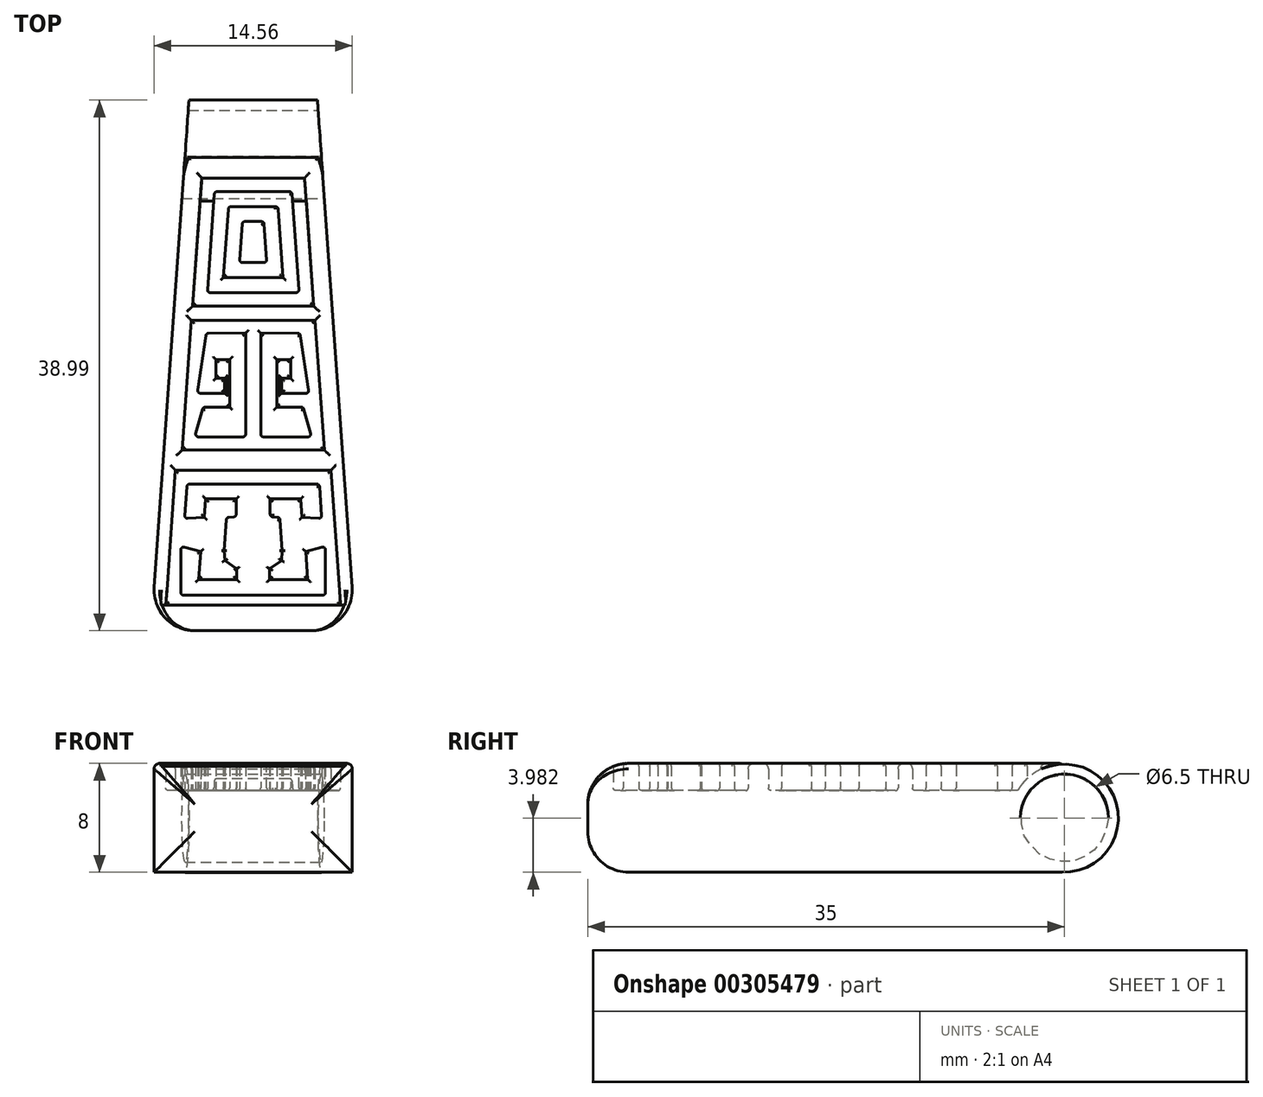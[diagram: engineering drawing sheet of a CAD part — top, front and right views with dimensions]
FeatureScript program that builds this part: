
annotation { "Feature Type Name" : "Feature", "Feature Type Description" : "" }
export const myFeature = defineFeature(function(context is Context, id is Id, definition is map)
    precondition{}
    {
        {
            var Q0;
            Q0=qCreatedBy(makeId("Top.planeOp"),FACE);
            var sketch = newSketch(context, id + "F0", { "sketchPlane" : qUnion([Q0])});
            skLineSegment(sketch, "E0", {"start": v(0, 0) * mm, "end": v(5, 0) * mm});
            skLineSegment(sketch, "E1", {"start": v(5, 0) * mm, "end": v(7.5, -35) * mm});
            skLineSegment(sketch, "E2", {"start": v(7.5, -35) * mm, "end": v(0, -35) * mm});
            skLineSegment(sketch, "E3", {"start": v(0, 0) * mm, "end": v(0, -35) * mm, "construction": true});
            skLineSegment(sketch, "E4", {"start": v(0, -1.73) * mm, "end": v(3.77, -1.73) * mm});
            skLineSegment(sketch, "E5", {"start": v(3.77, -1.73) * mm, "end": v(4.44, -11.15) * mm});
            skLineSegment(sketch, "E6", {"start": v(4.44, -11.15) * mm, "end": v(0, -11.15) * mm});
            skLineSegment(sketch, "E7", {"start": v(0, -12.2) * mm, "end": v(4.54, -12.2) * mm});
            skLineSegment(sketch, "E8", {"start": v(4.54, -12.2) * mm, "end": v(5.22, -21.73) * mm});
            skLineSegment(sketch, "E9", {"start": v(5.22, -21.73) * mm, "end": v(0, -21.73) * mm});
            skLineSegment(sketch, "E10", {"start": v(0, -23.21) * mm, "end": v(5.7, -23.21) * mm});
            skLineSegment(sketch, "E11", {"start": v(5.7, -23.21) * mm, "end": v(6.42, -33.12) * mm});
            skLineSegment(sketch, "E12", {"start": v(6.42, -33.12) * mm, "end": v(0, -33.12) * mm});
            skLineSegment(sketch, "E13.MirrorCS", {"start": v(0, 0) * mm, "end": v(-5, 0) * mm});
            skLineSegment(sketch, "E14.MirrorCS", {"start": v(-4.44, -11.15) * mm, "end": v(0, -11.15) * mm});
            skLineSegment(sketch, "E15.MirrorCS", {"start": v(-7.5, -35) * mm, "end": v(0, -35) * mm});
            skLineSegment(sketch, "E16.MirrorCS", {"start": v(-6.42, -33.12) * mm, "end": v(0, -33.12) * mm});
            skLineSegment(sketch, "E17.MirrorCS", {"start": v(-5.7, -23.21) * mm, "end": v(-6.42, -33.12) * mm});
            skLineSegment(sketch, "E18.MirrorCS", {"start": v(-5, 0) * mm, "end": v(-7.5, -35) * mm});
            skLineSegment(sketch, "E19.MirrorCS", {"start": v(0, -23.21) * mm, "end": v(-5.7, -23.21) * mm});
            skLineSegment(sketch, "E20.MirrorCS", {"start": v(-3.77, -1.73) * mm, "end": v(-4.44, -11.15) * mm});
            skLineSegment(sketch, "E21.MirrorCS", {"start": v(-5.22, -21.73) * mm, "end": v(0, -21.73) * mm});
            skLineSegment(sketch, "E22.MirrorCS", {"start": v(0, -12.2) * mm, "end": v(-4.54, -12.2) * mm});
            skLineSegment(sketch, "E23.MirrorCS", {"start": v(-4.54, -12.2) * mm, "end": v(-5.22, -21.73) * mm});
            skLineSegment(sketch, "E24.MirrorCS", {"start": v(0, -1.73) * mm, "end": v(-3.77, -1.73) * mm});
            skLineSegment(sketch, "E25.0", {"start": v(0, -2.73) * mm, "end": v(2.84, -2.73) * mm});
            skLineSegment(sketch, "E25.1", {"start": v(-2.84, -2.73) * mm, "end": v(-3.37, -10.15) * mm});
            skLineSegment(sketch, "E25.2", {"start": v(-3.37, -10.15) * mm, "end": v(0, -10.15) * mm});
            skLineSegment(sketch, "E25.3", {"start": v(0, -2.73) * mm, "end": v(-2.84, -2.73) * mm});
            skLineSegment(sketch, "E25.4", {"start": v(3.37, -10.15) * mm, "end": v(0, -10.15) * mm});
            skLineSegment(sketch, "E25.5", {"start": v(2.84, -2.73) * mm, "end": v(3.37, -10.15) * mm});
            skLineSegment(sketch, "E26.0", {"start": v(0, -3.83) * mm, "end": v(-1.82, -3.83) * mm});
            skLineSegment(sketch, "E26.1", {"start": v(1.82, -3.83) * mm, "end": v(2.19, -9.05) * mm});
            skLineSegment(sketch, "E26.2", {"start": v(2.19, -9.05) * mm, "end": v(0.29, -9.05) * mm});
            skLineSegment(sketch, "E26.3", {"start": v(0, -3.83) * mm, "end": v(1.82, -3.83) * mm});
            skLineSegment(sketch, "E26.4", {"start": v(-2.19, -9.05) * mm, "end": v(0.29, -9.05) * mm});
            skLineSegment(sketch, "E26.5", {"start": v(-1.82, -3.83) * mm, "end": v(-2.19, -9.05) * mm});
            skLineSegment(sketch, "E27", {"start": v(0.55, -13.13) * mm, "end": v(0.55, -20.76) * mm});
            skLineSegment(sketch, "E28", {"start": v(0.55, -20.76) * mm, "end": v(4.28, -20.76) * mm});
            skLineSegment(sketch, "E29", {"start": v(4.28, -20.76) * mm, "end": v(3.68, -18.57) * mm});
            skLineSegment(sketch, "E30", {"start": v(3.68, -18.57) * mm, "end": v(1.73, -18.57) * mm});
            skLineSegment(sketch, "E31", {"start": v(1.73, -18.57) * mm, "end": v(1.73, -15.07) * mm});
            skLineSegment(sketch, "E32", {"start": v(1.73, -15.07) * mm, "end": v(2.74, -15.07) * mm});
            skLineSegment(sketch, "E33", {"start": v(2.74, -15.07) * mm, "end": v(2.74, -16.45) * mm});
            skLineSegment(sketch, "E34", {"start": v(2.74, -16.45) * mm, "end": v(2.09, -16.45) * mm});
            skLineSegment(sketch, "E35", {"start": v(2.09, -16.45) * mm, "end": v(2.09, -17.55) * mm});
            skLineSegment(sketch, "E36", {"start": v(2.09, -17.55) * mm, "end": v(4.1, -17.55) * mm});
            skLineSegment(sketch, "E37", {"start": v(4.1, -17.55) * mm, "end": v(3.44, -13.14) * mm});
            skLineSegment(sketch, "E38", {"start": v(3.44, -13.14) * mm, "end": v(0.55, -13.13) * mm});
            skLineSegment(sketch, "E39.MirrorCS", {"start": v(-1.73, -15.07) * mm, "end": v(-2.74, -15.07) * mm});
            skLineSegment(sketch, "E40.MirrorCS", {"start": v(-0.55, -20.76) * mm, "end": v(-4.28, -20.76) * mm});
            skLineSegment(sketch, "E41.MirrorCS", {"start": v(-4.1, -17.55) * mm, "end": v(-3.44, -13.14) * mm});
            skLineSegment(sketch, "E42.MirrorCS", {"start": v(-1.73, -18.57) * mm, "end": v(-1.73, -15.07) * mm});
            skLineSegment(sketch, "E43.MirrorCS", {"start": v(-2.09, -17.55) * mm, "end": v(-4.1, -17.55) * mm});
            skLineSegment(sketch, "E44.MirrorCS", {"start": v(-3.44, -13.14) * mm, "end": v(-0.55, -13.13) * mm});
            skLineSegment(sketch, "E45.MirrorCS", {"start": v(-2.09, -16.45) * mm, "end": v(-2.09, -17.55) * mm});
            skLineSegment(sketch, "E46.MirrorCS", {"start": v(-2.74, -15.07) * mm, "end": v(-2.74, -16.45) * mm});
            skLineSegment(sketch, "E47.MirrorCS", {"start": v(-0.55, -13.13) * mm, "end": v(-0.55, -20.76) * mm});
            skLineSegment(sketch, "E48.MirrorCS", {"start": v(-3.68, -18.57) * mm, "end": v(-1.73, -18.57) * mm});
            skLineSegment(sketch, "E49.MirrorCS", {"start": v(-2.74, -16.45) * mm, "end": v(-2.09, -16.45) * mm});
            skLineSegment(sketch, "E50.MirrorCS", {"start": v(-4.28, -20.76) * mm, "end": v(-3.68, -18.57) * mm});
            skLineSegment(sketch, "E51", {"start": v(0, -24.23) * mm, "end": v(4.86, -24.23) * mm});
            skLineSegment(sketch, "E52", {"start": v(4.86, -24.23) * mm, "end": v(5.04, -26.76) * mm});
            skLineSegment(sketch, "E53", {"start": v(5.04, -26.76) * mm, "end": v(3.6, -26.66) * mm});
            skLineSegment(sketch, "E54", {"start": v(3.6, -26.66) * mm, "end": v(3.5, -25.32) * mm});
            skLineSegment(sketch, "E55", {"start": v(3.5, -25.32) * mm, "end": v(1.25, -25.32) * mm});
            skLineSegment(sketch, "E56", {"start": v(1.25, -25.32) * mm, "end": v(1.25, -26.62) * mm});
            skLineSegment(sketch, "E57", {"start": v(1.25, -26.62) * mm, "end": v(1.96, -26.67) * mm});
            skLineSegment(sketch, "E58", {"start": v(1.96, -26.67) * mm, "end": v(2.13, -29.11) * mm});
            skLineSegment(sketch, "E59", {"start": v(2.13, -29.11) * mm, "end": v(2.08, -29.84) * mm});
            skLineSegment(sketch, "E60", {"start": v(2.08, -29.84) * mm, "end": v(1.2, -30.44) * mm});
            skLineSegment(sketch, "E61", {"start": v(1.2, -30.44) * mm, "end": v(1.2, -31.23) * mm});
            skLineSegment(sketch, "E62", {"start": v(1.2, -31.23) * mm, "end": v(4, -31.23) * mm});
            skLineSegment(sketch, "E63", {"start": v(4, -31.23) * mm, "end": v(3.86, -29.17) * mm});
            skLineSegment(sketch, "E64", {"start": v(3.86, -29.17) * mm, "end": v(5.3, -28.8) * mm});
            skLineSegment(sketch, "E65", {"start": v(5.3, -28.8) * mm, "end": v(5.3, -32.4) * mm});
            skLineSegment(sketch, "E66", {"start": v(5.3, -32.4) * mm, "end": v(0, -32.4) * mm});
            skLineSegment(sketch, "E67.MirrorCS", {"start": v(-1.25, -26.62) * mm, "end": v(-1.96, -26.67) * mm});
            skLineSegment(sketch, "E68.MirrorCS", {"start": v(-5.3, -28.8) * mm, "end": v(-5.3, -32.4) * mm});
            skLineSegment(sketch, "E69.MirrorCS", {"start": v(-1.96, -26.67) * mm, "end": v(-2.13, -29.11) * mm});
            skLineSegment(sketch, "E70.MirrorCS", {"start": v(-3.86, -29.17) * mm, "end": v(-5.3, -28.8) * mm});
            skLineSegment(sketch, "E71.MirrorCS", {"start": v(-4, -31.23) * mm, "end": v(-3.86, -29.17) * mm});
            skLineSegment(sketch, "E72.MirrorCS", {"start": v(-4.86, -24.23) * mm, "end": v(-5.04, -26.76) * mm});
            skLineSegment(sketch, "E73.MirrorCS", {"start": v(-2.13, -29.11) * mm, "end": v(-2.08, -29.84) * mm});
            skLineSegment(sketch, "E74.MirrorCS", {"start": v(-1.25, -25.32) * mm, "end": v(-1.25, -26.62) * mm});
            skLineSegment(sketch, "E75.MirrorCS", {"start": v(-1.2, -30.44) * mm, "end": v(-1.2, -31.23) * mm});
            skLineSegment(sketch, "E76.MirrorCS", {"start": v(-3.6, -26.66) * mm, "end": v(-3.5, -25.32) * mm});
            skLineSegment(sketch, "E77.MirrorCS", {"start": v(-5.04, -26.76) * mm, "end": v(-3.6, -26.66) * mm});
            skLineSegment(sketch, "E78.MirrorCS", {"start": v(-2.08, -29.84) * mm, "end": v(-1.2, -30.44) * mm});
            skLineSegment(sketch, "E79.MirrorCS", {"start": v(-1.2, -31.23) * mm, "end": v(-4, -31.23) * mm});
            skLineSegment(sketch, "E80.MirrorCS", {"start": v(-3.5, -25.32) * mm, "end": v(-1.25, -25.32) * mm});
            skLineSegment(sketch, "E81.MirrorCS", {"start": v(0, -24.23) * mm, "end": v(-4.86, -24.23) * mm});
            skLineSegment(sketch, "E82.MirrorCS", {"start": v(-5.3, -32.4) * mm, "end": v(0, -32.4) * mm});
            skLineSegment(sketch, "E83.0", {"start": v(0, -4.93) * mm, "end": v(0.8, -4.93) * mm});
            skLineSegment(sketch, "E83.1", {"start": v(-0.8, -4.93) * mm, "end": v(-1, -7.95) * mm});
            skLineSegment(sketch, "E83.2", {"start": v(-1, -7.95) * mm, "end": v(0, -7.95) * mm});
            skLineSegment(sketch, "E83.3", {"start": v(0, -4.93) * mm, "end": v(-0.8, -4.93) * mm});
            skLineSegment(sketch, "E83.4", {"start": v(1, -7.95) * mm, "end": v(0, -7.95) * mm});
            skLineSegment(sketch, "E83.5", {"start": v(0.8, -4.93) * mm, "end": v(1, -7.95) * mm});
            skSolve(sketch);
        }
        {
            var Q0;
            Q0=makeQuery(id+"F0.imprint","IMPRINT",FACE,{"disambiguationData":[TD([[makeQuery(id+"F0.imprint","IMPRINT",EDGE,{"derivedFrom":sQuery(id+"F0.wireOp",EDGE,"E0")}),-1.0]])]});
            var Q1;
            Q1=makeQuery(id+"F0.imprint","IMPRINT",FACE,{"disambiguationData":[TD([[makeQuery(id+"F0.imprint","IMPRINT",EDGE,{"derivedFrom":sQuery(id+"F0.wireOp",EDGE,"E7")}),-1.0]])]});
            var Q2;
            Q2=makeQuery(id+"F0.imprint","IMPRINT",FACE,{"disambiguationData":[TD([[makeQuery(id+"F0.imprint","IMPRINT",EDGE,{"derivedFrom":sQuery(id+"F0.wireOp",EDGE,"E25.0")}),-1.0]])]});
            var Q3;
            Q3=makeQuery(id+"F0.imprint","IMPRINT",FACE,{"disambiguationData":[TD([[makeQuery(id+"F0.imprint","IMPRINT",EDGE,{"derivedFrom":sQuery(id+"F0.wireOp",EDGE,"E26.0")}),1.0]])]});
            var Q4;
            Q4=makeQuery(id+"F0.imprint","IMPRINT",FACE,{"disambiguationData":[TD([[makeQuery(id+"F0.imprint","IMPRINT",EDGE,{"derivedFrom":sQuery(id+"F0.wireOp",EDGE,"E27")}),1.0]])]});
            var Q5;
            Q5=makeQuery(id+"F0.imprint","IMPRINT",FACE,{"disambiguationData":[TD([[makeQuery(id+"F0.imprint","IMPRINT",EDGE,{"derivedFrom":sQuery(id+"F0.wireOp",EDGE,"E39.MirrorCS")}),-1.0]])]});
            var Q6;
            Q6=makeQuery(id+"F0.imprint","IMPRINT",FACE,{"disambiguationData":[TD([[makeQuery(id+"F0.imprint","IMPRINT",EDGE,{"derivedFrom":sQuery(id+"F0.wireOp",EDGE,"E51")}),-1.0]])]});
            var Q7;
            Q7=makeQuery(id+"F0.imprint","IMPRINT",FACE,{"disambiguationData":[TD([[makeQuery(id+"F0.imprint","IMPRINT",EDGE,{"derivedFrom":sQuery(id+"F0.wireOp",EDGE,"E4")}),-1.0]])]});
            var Q8;
            Q8=makeQuery(id+"F0.imprint","IMPRINT",FACE,{"disambiguationData":[TD([[makeQuery(id+"F0.imprint","IMPRINT",EDGE,{"derivedFrom":sQuery(id+"F0.wireOp",EDGE,"E10")}),-1.0]])]});
            var Q9;
            Q9=makeQuery(id+"F0.imprint","IMPRINT",FACE,{"disambiguationData":[TD([[makeQuery(id+"F0.imprint","IMPRINT",EDGE,{"derivedFrom":sQuery(id+"F0.wireOp",EDGE,"E83.0")}),-1.0]])]});
            extrude(context, id + "F1", {"entities" : qUnion([Q0, Q1, Q2, Q3, Q4, Q5, Q6, Q7, Q8, Q9]), "oppositeDirection" : true, "depth" : 6 * mm});
        }
        {
            var Q0;
            Q0 = qSketchRegion(id + "F0", true);
            var Q1;
            Q1=makeQuery(id+"F0.imprint","IMPRINT",FACE,{"disambiguationData":[TD([[makeQuery(id+"F0.imprint","IMPRINT",EDGE,{"derivedFrom":sQuery(id+"F0.wireOp",EDGE,"E83.0")}),-1.0]])]});
            extrude(context, id + "F2", {"entities" : qUnion([Q0, Q1]), "operationType" : NewBodyOperationType.ADD, "depth" : 2 * mm});
        }
        {
            var Q0;
            Q0=makeQuery(id+"F0.imprint","IMPRINT",FACE,{"disambiguationData":[TD([[makeQuery(id+"F0.imprint","IMPRINT",EDGE,{"derivedFrom":sQuery(id+"F0.wireOp",EDGE,"E25.0")}),-1.0]])]});
            var Q1;
            Q1=makeQuery(id+"F0.imprint","IMPRINT",FACE,{"disambiguationData":[TD([[makeQuery(id+"F0.imprint","IMPRINT",EDGE,{"derivedFrom":sQuery(id+"F0.wireOp",EDGE,"E27")}),1.0]])]});
            var Q2;
            Q2=makeQuery(id+"F0.imprint","IMPRINT",FACE,{"disambiguationData":[TD([[makeQuery(id+"F0.imprint","IMPRINT",EDGE,{"derivedFrom":sQuery(id+"F0.wireOp",EDGE,"E39.MirrorCS")}),-1.0]])]});
            var Q3;
            Q3=makeQuery(id+"F0.imprint","IMPRINT",FACE,{"disambiguationData":[TD([[makeQuery(id+"F0.imprint","IMPRINT",EDGE,{"derivedFrom":sQuery(id+"F0.wireOp",EDGE,"E51")}),-1.0]])]});
            extrude(context, id + "F3", {"entities" : qUnion([Q0, Q1, Q2, Q3]), "operationType" : NewBodyOperationType.ADD, "depth" : 2 * mm});
        }
        {
            var Q0;
            {var subQ0=sQuery(id+"F0.wireOp",EDGE,"E15.MirrorCS");var subQ1=sQuery(id+"F0.wireOp",EDGE,"E2");Q0=makeQuery(id+"F2.boolean.opBoolean","MERGE",FACE,{"derivedFrom":[makeQuery(id+"F1.opExtrude","SWEPT_FACE",FACE,{"disambiguationData":[OSD([subQ1,subQ0])]}),makeQuery(id+"F2.opExtrude","SWEPT_FACE",FACE,{"disambiguationData":[OSD([subQ1,subQ0])]})]});}
            fillet(context, id + "F4", {"entities" : qUnion([Q0]), "radius" : 3 * mm, "tangentPropagation" : true, "allowEdgeOverflow" : false});
        }
        {
            var Q0;
            Q0=makeQuery(id+"F3.opExtrude","CAP_FACE",FACE,{"disambiguationData":[OSD([sQuery(id+"F0.wireOp",EDGE,"E51"),sQuery(id+"F0.wireOp",EDGE,"E52"),sQuery(id+"F0.wireOp",EDGE,"E53"),sQuery(id+"F0.wireOp",EDGE,"E54"),sQuery(id+"F0.wireOp",EDGE,"E55"),sQuery(id+"F0.wireOp",EDGE,"E56"),sQuery(id+"F0.wireOp",EDGE,"E57"),sQuery(id+"F0.wireOp",EDGE,"E58"),sQuery(id+"F0.wireOp",EDGE,"E59"),sQuery(id+"F0.wireOp",EDGE,"E60"),sQuery(id+"F0.wireOp",EDGE,"E61"),sQuery(id+"F0.wireOp",EDGE,"E62"),sQuery(id+"F0.wireOp",EDGE,"E63"),sQuery(id+"F0.wireOp",EDGE,"E64"),sQuery(id+"F0.wireOp",EDGE,"E65"),sQuery(id+"F0.wireOp",EDGE,"E66"),sQuery(id+"F0.wireOp",EDGE,"E67.MirrorCS"),sQuery(id+"F0.wireOp",EDGE,"E68.MirrorCS"),sQuery(id+"F0.wireOp",EDGE,"E69.MirrorCS"),sQuery(id+"F0.wireOp",EDGE,"E70.MirrorCS"),sQuery(id+"F0.wireOp",EDGE,"E71.MirrorCS"),sQuery(id+"F0.wireOp",EDGE,"E72.MirrorCS"),sQuery(id+"F0.wireOp",EDGE,"E73.MirrorCS"),sQuery(id+"F0.wireOp",EDGE,"E74.MirrorCS"),sQuery(id+"F0.wireOp",EDGE,"E75.MirrorCS"),sQuery(id+"F0.wireOp",EDGE,"E76.MirrorCS"),sQuery(id+"F0.wireOp",EDGE,"E77.MirrorCS"),sQuery(id+"F0.wireOp",EDGE,"E78.MirrorCS"),sQuery(id+"F0.wireOp",EDGE,"E79.MirrorCS"),sQuery(id+"F0.wireOp",EDGE,"E80.MirrorCS"),sQuery(id+"F0.wireOp",EDGE,"E81.MirrorCS"),sQuery(id+"F0.wireOp",EDGE,"E82.MirrorCS")])],"isStart":false});
            var Q1;
            Q1=makeQuery(id+"F3.opExtrude","CAP_FACE",FACE,{"disambiguationData":[OSD([sQuery(id+"F0.wireOp",EDGE,"E27"),sQuery(id+"F0.wireOp",EDGE,"E28"),sQuery(id+"F0.wireOp",EDGE,"E29"),sQuery(id+"F0.wireOp",EDGE,"E30"),sQuery(id+"F0.wireOp",EDGE,"E31"),sQuery(id+"F0.wireOp",EDGE,"E32"),sQuery(id+"F0.wireOp",EDGE,"E33"),sQuery(id+"F0.wireOp",EDGE,"E34"),sQuery(id+"F0.wireOp",EDGE,"E35"),sQuery(id+"F0.wireOp",EDGE,"E36"),sQuery(id+"F0.wireOp",EDGE,"E37"),sQuery(id+"F0.wireOp",EDGE,"E38")])],"isStart":false});
            var Q2;
            Q2=makeQuery(id+"F3.opExtrude","CAP_FACE",FACE,{"disambiguationData":[OSD([sQuery(id+"F0.wireOp",EDGE,"E39.MirrorCS"),sQuery(id+"F0.wireOp",EDGE,"E40.MirrorCS"),sQuery(id+"F0.wireOp",EDGE,"E41.MirrorCS"),sQuery(id+"F0.wireOp",EDGE,"E42.MirrorCS"),sQuery(id+"F0.wireOp",EDGE,"E43.MirrorCS"),sQuery(id+"F0.wireOp",EDGE,"E44.MirrorCS"),sQuery(id+"F0.wireOp",EDGE,"E45.MirrorCS"),sQuery(id+"F0.wireOp",EDGE,"E46.MirrorCS"),sQuery(id+"F0.wireOp",EDGE,"E47.MirrorCS"),sQuery(id+"F0.wireOp",EDGE,"E48.MirrorCS"),sQuery(id+"F0.wireOp",EDGE,"E49.MirrorCS"),sQuery(id+"F0.wireOp",EDGE,"E50.MirrorCS")])],"isStart":false});
            var Q3;
            Q3=makeQuery(id+"F3.opExtrude","CAP_FACE",FACE,{"disambiguationData":[OSD([sQuery(id+"F0.wireOp",EDGE,"E25.0"),sQuery(id+"F0.wireOp",EDGE,"E25.1"),sQuery(id+"F0.wireOp",EDGE,"E25.2"),sQuery(id+"F0.wireOp",EDGE,"E25.3"),sQuery(id+"F0.wireOp",EDGE,"E25.4"),sQuery(id+"F0.wireOp",EDGE,"E25.5"),sQuery(id+"F0.wireOp",EDGE,"E26.0"),sQuery(id+"F0.wireOp",EDGE,"E26.1"),sQuery(id+"F0.wireOp",EDGE,"E26.2"),sQuery(id+"F0.wireOp",EDGE,"E26.3"),sQuery(id+"F0.wireOp",EDGE,"E26.4"),sQuery(id+"F0.wireOp",EDGE,"E26.5")])],"isStart":false});
            var Q4;
            Q4=makeQuery(id+"F2.boolean.opBoolean","SPLIT",FACE,{"disambiguationData":[TD([makeQuery(id+"F2.opExtrude","SWEPT_FACE",FACE,{"disambiguationData":[OSD([sQuery(id+"F0.wireOp",EDGE,"E8")])]})])],"derivedFrom":makeQuery(id+"F1.opExtrude","CAP_FACE",FACE,{"disambiguationData":[OSD([sQuery(id+"F0.wireOp",EDGE,"E0"),sQuery(id+"F0.wireOp",EDGE,"E1"),sQuery(id+"F0.wireOp",EDGE,"E2"),sQuery(id+"F0.wireOp",EDGE,"E13.MirrorCS"),sQuery(id+"F0.wireOp",EDGE,"E15.MirrorCS"),sQuery(id+"F0.wireOp",EDGE,"E18.MirrorCS")])],"isStart":true})});
            var Q5;
            {var subQ3=makeQuery(id+"F2.opExtrude","SWEPT_FACE",FACE,{"disambiguationData":[OSD([sQuery(id+"F0.wireOp",EDGE,"E5")])]});Q5=makeQuery(id+"F3.boolean.opBoolean","SPLIT",FACE,{"disambiguationData":[TD([subQ3])],"derivedFrom":makeQuery(id+"F2.boolean.opBoolean","SPLIT",FACE,{"disambiguationData":[TD([subQ3])],"derivedFrom":makeQuery(id+"F1.opExtrude","CAP_FACE",FACE,{"disambiguationData":[OSD([sQuery(id+"F0.wireOp",EDGE,"E0"),sQuery(id+"F0.wireOp",EDGE,"E1"),sQuery(id+"F0.wireOp",EDGE,"E2"),sQuery(id+"F0.wireOp",EDGE,"E13.MirrorCS"),sQuery(id+"F0.wireOp",EDGE,"E15.MirrorCS"),sQuery(id+"F0.wireOp",EDGE,"E18.MirrorCS")])],"isStart":true})})});}
            var Q6;
            Q6=makeQuery(id+"F2.boolean.opBoolean","SPLIT",FACE,{"disambiguationData":[TD([makeQuery(id+"F2.opExtrude","SWEPT_FACE",FACE,{"disambiguationData":[OSD([sQuery(id+"F0.wireOp",EDGE,"E11")])]})])],"derivedFrom":makeQuery(id+"F1.opExtrude","CAP_FACE",FACE,{"disambiguationData":[OSD([sQuery(id+"F0.wireOp",EDGE,"E0"),sQuery(id+"F0.wireOp",EDGE,"E1"),sQuery(id+"F0.wireOp",EDGE,"E2"),sQuery(id+"F0.wireOp",EDGE,"E13.MirrorCS"),sQuery(id+"F0.wireOp",EDGE,"E15.MirrorCS"),sQuery(id+"F0.wireOp",EDGE,"E18.MirrorCS")])],"isStart":true})});
            var Q7;
            Q7=makeQuery(id+"F3.opExtrude","SWEPT_FACE",FACE,{"disambiguationData":[OSD([sQuery(id+"F0.wireOp",EDGE,"E29")])]});
            var Q8;
            Q8=makeQuery(id+"F3.opExtrude","SWEPT_FACE",FACE,{"disambiguationData":[OSD([sQuery(id+"F0.wireOp",EDGE,"E37")])]});
            var Q9;
            Q9=makeQuery(id+"F3.opExtrude","SWEPT_FACE",FACE,{"disambiguationData":[OSD([sQuery(id+"F0.wireOp",EDGE,"E52")])]});
            var Q10;
            Q10=makeQuery(id+"F3.opExtrude","SWEPT_FACE",FACE,{"disambiguationData":[OSD([sQuery(id+"F0.wireOp",EDGE,"E65")])]});
            var Q11;
            Q11=makeQuery(id+"F3.opExtrude","SWEPT_FACE",FACE,{"disambiguationData":[OSD([sQuery(id+"F0.wireOp",EDGE,"E25.5")])]});
            var Q12;
            Q12=makeQuery(id+"F3.opExtrude","SWEPT_FACE",FACE,{"disambiguationData":[OSD([sQuery(id+"F0.wireOp",EDGE,"E25.1")])]});
            var Q13;
            Q13=makeQuery(id+"F3.opExtrude","SWEPT_FACE",FACE,{"disambiguationData":[OSD([sQuery(id+"F0.wireOp",EDGE,"E41.MirrorCS")])]});
            var Q14;
            Q14=makeQuery(id+"F3.opExtrude","SWEPT_FACE",FACE,{"disambiguationData":[OSD([sQuery(id+"F0.wireOp",EDGE,"E50.MirrorCS")])]});
            var Q15;
            Q15=makeQuery(id+"F3.opExtrude","SWEPT_FACE",FACE,{"disambiguationData":[OSD([sQuery(id+"F0.wireOp",EDGE,"E72.MirrorCS")])]});
            var Q16;
            Q16=makeQuery(id+"F3.opExtrude","SWEPT_FACE",FACE,{"disambiguationData":[OSD([sQuery(id+"F0.wireOp",EDGE,"E68.MirrorCS")])]});
            var Q17;
            Q17=makeQuery(id+"F3.opExtrude","SWEPT_EDGE",EDGE,{"disambiguationData":[OSD([sQuery(id+"F0.wireOp",EDGE,"E27"),sQuery(id+"F0.wireOp",EDGE,"E28")])]});
            var Q18;
            Q18=makeQuery(id+"F3.opExtrude","SWEPT_EDGE",EDGE,{"disambiguationData":[OSD([sQuery(id+"F0.wireOp",EDGE,"E40.MirrorCS"),sQuery(id+"F0.wireOp",EDGE,"E47.MirrorCS")])]});
            var Q19;
            Q19=makeQuery(id+"F2.opExtrude","CAP_FACE",FACE,{"disambiguationData":[OSD([sQuery(id+"F0.wireOp",EDGE,"E83.0"),sQuery(id+"F0.wireOp",EDGE,"E83.1"),sQuery(id+"F0.wireOp",EDGE,"E83.2"),sQuery(id+"F0.wireOp",EDGE,"E83.3"),sQuery(id+"F0.wireOp",EDGE,"E83.4"),sQuery(id+"F0.wireOp",EDGE,"E83.5")])],"isStart":false});
            var Q20;
            Q20=makeQuery(id+"F2.opExtrude","SWEPT_EDGE",EDGE,{"disambiguationData":[OSD([sQuery(id+"F0.wireOp",EDGE,"E83.4"),sQuery(id+"F0.wireOp",EDGE,"E83.5")])]});
            var Q21;
            Q21=makeQuery(id+"F2.opExtrude","SWEPT_EDGE",EDGE,{"disambiguationData":[OSD([sQuery(id+"F0.wireOp",EDGE,"E83.1"),sQuery(id+"F0.wireOp",EDGE,"E83.2")])]});
            var Q22;
            Q22=makeQuery(id+"F3.opExtrude","SWEPT_FACE",FACE,{"disambiguationData":[OSD([sQuery(id+"F0.wireOp",EDGE,"E26.0"),sQuery(id+"F0.wireOp",EDGE,"E26.3")])]});
            var Q23;
            {var subQ2=makeQuery(id+"F2.opExtrude","SWEPT_FACE",FACE,{"disambiguationData":[OSD([sQuery(id+"F0.wireOp",EDGE,"E83.1")])]});Q23=makeQuery(id+"F3.boolean.opBoolean","SPLIT",FACE,{"disambiguationData":[TD([subQ2])],"derivedFrom":makeQuery(id+"F2.boolean.opBoolean","SPLIT",FACE,{"disambiguationData":[TD([makeQuery(id+"F2.opExtrude","SWEPT_FACE",FACE,{"disambiguationData":[OSD([sQuery(id+"F0.wireOp",EDGE,"E5")])]})])],"derivedFrom":makeQuery(id+"F1.opExtrude","CAP_FACE",FACE,{"disambiguationData":[OSD([sQuery(id+"F0.wireOp",EDGE,"E0"),sQuery(id+"F0.wireOp",EDGE,"E1"),sQuery(id+"F0.wireOp",EDGE,"E2"),sQuery(id+"F0.wireOp",EDGE,"E13.MirrorCS"),sQuery(id+"F0.wireOp",EDGE,"E15.MirrorCS"),sQuery(id+"F0.wireOp",EDGE,"E18.MirrorCS")])],"isStart":true})})});}
            var Q24;
            Q24=makeQuery(id+"F2.opExtrude","SWEPT_FACE",FACE,{"disambiguationData":[OSD([sQuery(id+"F0.wireOp",EDGE,"E83.0"),sQuery(id+"F0.wireOp",EDGE,"E83.3")])]});
            var Q25;
            Q25=makeQuery(id+"F3.opExtrude","SWEPT_EDGE",EDGE,{"disambiguationData":[OSD([sQuery(id+"F0.wireOp",EDGE,"E57"),sQuery(id+"F0.wireOp",EDGE,"E58")])]});
            var Q26;
            Q26=makeQuery(id+"F3.opExtrude","SWEPT_EDGE",EDGE,{"disambiguationData":[OSD([sQuery(id+"F0.wireOp",EDGE,"E56"),sQuery(id+"F0.wireOp",EDGE,"E57")])]});
            var Q27;
            Q27=makeQuery(id+"F3.opExtrude","SWEPT_EDGE",EDGE,{"disambiguationData":[OSD([sQuery(id+"F0.wireOp",EDGE,"E67.MirrorCS"),sQuery(id+"F0.wireOp",EDGE,"E74.MirrorCS")])]});
            var Q28;
            Q28=makeQuery(id+"F3.opExtrude","SWEPT_EDGE",EDGE,{"disambiguationData":[OSD([sQuery(id+"F0.wireOp",EDGE,"E67.MirrorCS"),sQuery(id+"F0.wireOp",EDGE,"E69.MirrorCS")])]});
            fillet(context, id + "F5", {"entities" : qUnion([Q0, Q1, Q2, Q3, Q4, Q5, Q6, Q7, Q8, Q9, Q10, Q11, Q12, Q13, Q14, Q15, Q16, Q17, Q18, Q19, Q20, Q21, Q22, Q23, Q24, Q25, Q26, Q27, Q28]), "radius" : .2 * mm, "tangentPropagation" : true, "allowEdgeOverflow" : false});
        }
        {
            var Q0;
            Q0=makeQuery(id+"F2.opExtrude","CAP_FACE",FACE,{"disambiguationData":[OSD([sQuery(id+"F0.wireOp",EDGE,"E0"),sQuery(id+"F0.wireOp",EDGE,"E1"),sQuery(id+"F0.wireOp",EDGE,"E2"),sQuery(id+"F0.wireOp",EDGE,"E4"),sQuery(id+"F0.wireOp",EDGE,"E5"),sQuery(id+"F0.wireOp",EDGE,"E6"),sQuery(id+"F0.wireOp",EDGE,"E7"),sQuery(id+"F0.wireOp",EDGE,"E8"),sQuery(id+"F0.wireOp",EDGE,"E9"),sQuery(id+"F0.wireOp",EDGE,"E10"),sQuery(id+"F0.wireOp",EDGE,"E11"),sQuery(id+"F0.wireOp",EDGE,"E12"),sQuery(id+"F0.wireOp",EDGE,"E13.MirrorCS"),sQuery(id+"F0.wireOp",EDGE,"E14.MirrorCS"),sQuery(id+"F0.wireOp",EDGE,"E15.MirrorCS"),sQuery(id+"F0.wireOp",EDGE,"E16.MirrorCS"),sQuery(id+"F0.wireOp",EDGE,"E17.MirrorCS"),sQuery(id+"F0.wireOp",EDGE,"E18.MirrorCS"),sQuery(id+"F0.wireOp",EDGE,"E19.MirrorCS"),sQuery(id+"F0.wireOp",EDGE,"E20.MirrorCS"),sQuery(id+"F0.wireOp",EDGE,"E22.MirrorCS"),sQuery(id+"F0.wireOp",EDGE,"E23.MirrorCS"),sQuery(id+"F0.wireOp",EDGE,"E24.MirrorCS"),sQuery(id+"F0.wireOp",EDGE,"E21.MirrorCS")])],"isStart":false});
            fillet(context, id + "F6", {"entities" : qUnion([Q0]), "radius" : .4 * mm, "tangentPropagation" : true, "allowEdgeOverflow" : false});
        }
        {
            var Q0;
            Q0=qCreatedBy(makeId("Right.planeOp"),FACE);
            var sketch = newSketch(context, id + "F7", { "sketchPlane" : qUnion([Q0])});
            skLineSegment(sketch, "E84.0", {"start": v(0, -6) * mm, "end": v(0, 1.6) * mm});
            skCircle(sketch, "E85", {"center": v(0, -2.02) * mm, "radius": 3.25 * mm});
            skCircle(sketch, "E86", {"center": v(0, -2.02) * mm, "radius": 3.99 * mm});
            skSolve(sketch);
        }
        {
            var Q0;
            {var subQ0=sQuery(id+"F7.wireOp",EDGE,"E86");var subQ1=sQuery(id+"F7.wireOp",EDGE,"E84.0");var subQ2=makeQuery(id+"F7.imprint","INTERSECT",VERTEX,{"disambiguationData":[OD(0.0)],"derivedFrom":[subQ1,subQ0]});Q0=makeQuery(id+"F7.imprint","IMPRINT",FACE,{"disambiguationData":[TD([[makeQuery(id+"F7.imprint","IMPRINT",EDGE,{"disambiguationData":[TD([[subQ2,-1.0]])],"derivedFrom":subQ1}),-1.0]])]});}
            var Q1;
            {var subQ0=sQuery(id+"F7.wireOp",EDGE,"E86");var subQ1=sQuery(id+"F7.wireOp",EDGE,"E84.0");var subQ2=makeQuery(id+"F7.imprint","INTERSECT",VERTEX,{"disambiguationData":[OD(0.0)],"derivedFrom":[subQ1,subQ0]});Q1=makeQuery(id+"F7.imprint","IMPRINT",FACE,{"disambiguationData":[TD([[makeQuery(id+"F7.imprint","IMPRINT",EDGE,{"disambiguationData":[TD([[subQ2,-1.0]])],"derivedFrom":subQ1}),1.0]])]});}
            var Q2;
            Q2=makeQuery(id+"F7.imprint","IMPRINT",FACE,{"disambiguationData":[TD([[makeQuery(id+"F7.imprint","IMPRINT",EDGE,{"derivedFrom":sQuery(id+"F7.wireOp",EDGE,"E86")}),1.0]])]});
            var Q3;
            {var subQ0=sQuery(id+"F0.wireOp",EDGE,"E1");Q3=makeQuery(id+"F2.boolean.opBoolean","MERGE",FACE,{"derivedFrom":[makeQuery(id+"F1.opExtrude","SWEPT_FACE",FACE,{"disambiguationData":[OSD([subQ0])]}),makeQuery(id+"F2.opExtrude","SWEPT_FACE",FACE,{"disambiguationData":[OSD([subQ0])]})]});}
            var Q4;
            {var subQ0=sQuery(id+"F0.wireOp",EDGE,"E18.MirrorCS");Q4=makeQuery(id+"F2.boolean.opBoolean","MERGE",FACE,{"derivedFrom":[makeQuery(id+"F1.opExtrude","SWEPT_FACE",FACE,{"disambiguationData":[OSD([subQ0])]}),makeQuery(id+"F2.opExtrude","SWEPT_FACE",FACE,{"disambiguationData":[OSD([subQ0])]})]});}
            extrude(context, id + "F8", {"entities" : qUnion([Q0, Q1, Q2]), "operationType" : NewBodyOperationType.ADD, "endBound" : BoundingType.UP_TO_SURFACE, "endBoundEntityFace" : qUnion([Q3]), "depth" : 25 * mm, "hasSecondDirection" : true, "secondDirectionBound" : SecondDirectionBoundingType.UP_TO_SURFACE, "secondDirectionOppositeDirection" : true, "secondDirectionBoundEntityFace" : qUnion([Q4]), "secondDirectionDepth" : 25 * mm});
        }
        {
            var Q0;
            {var subQ0=sQuery(id+"F7.wireOp",EDGE,"E85");var subQ1=sQuery(id+"F7.wireOp",EDGE,"E84.0");var subQ2=makeQuery(id+"F7.imprint","INTERSECT",VERTEX,{"disambiguationData":[OD(0.0)],"derivedFrom":[subQ1,subQ0]});Q0=makeQuery(id+"F7.imprint","IMPRINT",FACE,{"disambiguationData":[TD([[makeQuery(id+"F7.imprint","IMPRINT",EDGE,{"disambiguationData":[TD([[subQ2,-1.0]])],"derivedFrom":subQ1}),-1.0]])]});}
            var Q1;
            {var subQ0=sQuery(id+"F7.wireOp",EDGE,"E85");var subQ1=sQuery(id+"F7.wireOp",EDGE,"E84.0");var subQ2=makeQuery(id+"F7.imprint","INTERSECT",VERTEX,{"disambiguationData":[OD(0.0)],"derivedFrom":[subQ1,subQ0]});Q1=makeQuery(id+"F7.imprint","IMPRINT",FACE,{"disambiguationData":[TD([[makeQuery(id+"F7.imprint","IMPRINT",EDGE,{"disambiguationData":[TD([[subQ2,-1.0]])],"derivedFrom":subQ1}),1.0]])]});}
            extrude(context, id + "F9", {"entities" : qUnion([Q0, Q1]), "operationType" : NewBodyOperationType.REMOVE, "oppositeDirection" : true, "depth" : 25 * mm, "hasSecondDirection" : true, "secondDirectionOppositeDirection" : false, "secondDirectionDepth" : 25 * mm});
        }
    });
